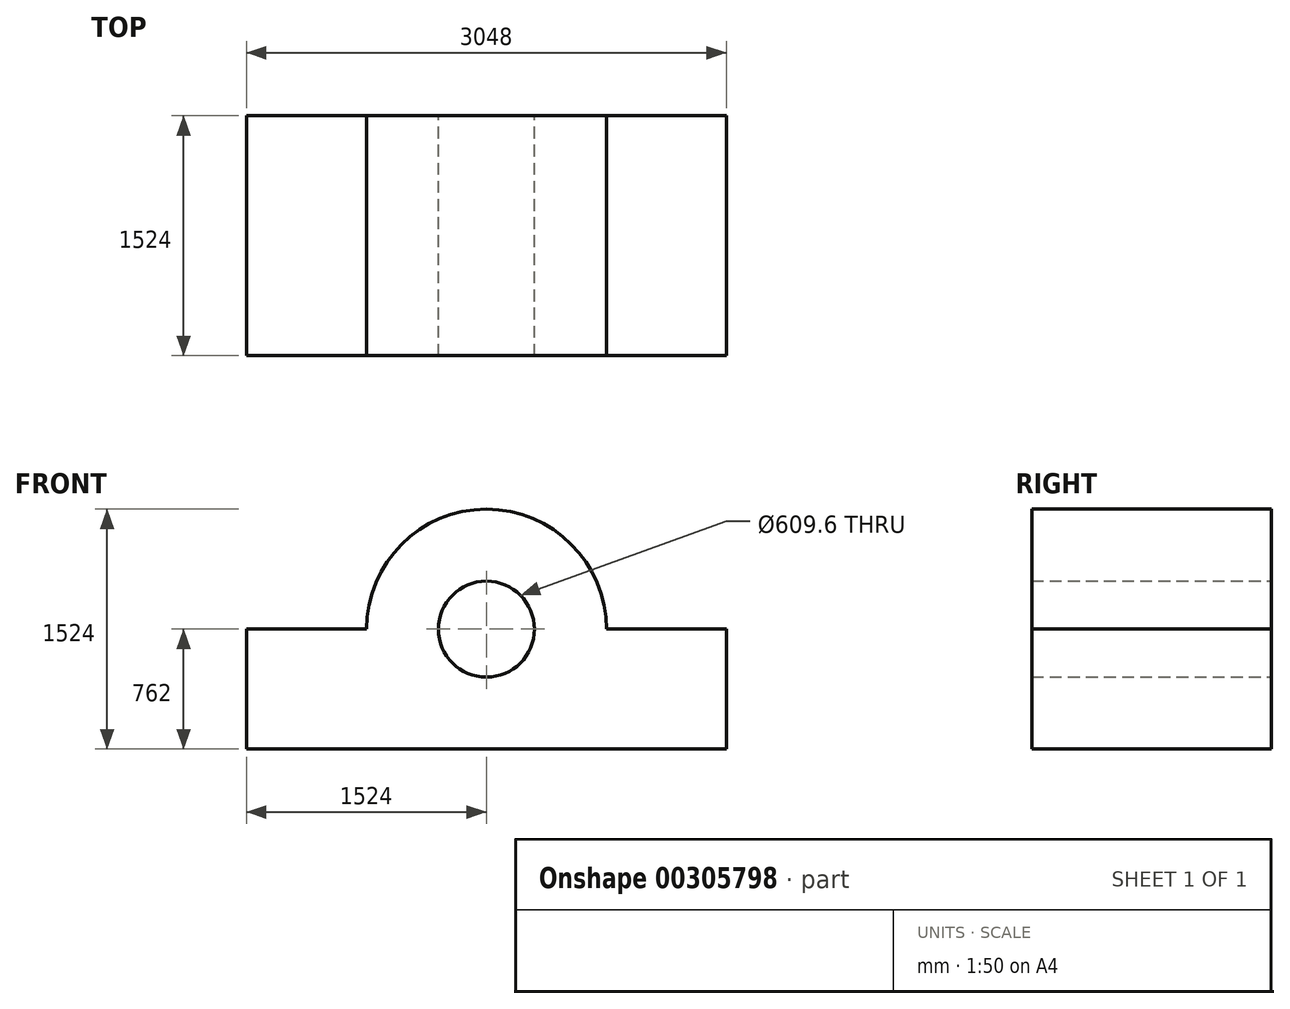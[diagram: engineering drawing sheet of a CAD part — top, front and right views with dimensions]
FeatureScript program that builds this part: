
annotation { "Feature Type Name" : "Feature", "Feature Type Description" : "" }
export const myFeature = defineFeature(function(context is Context, id is Id, definition is map)
    precondition{}
    {
        {
            var Q0;
            Q0=qCreatedBy(makeId("Front.planeOp"),FACE);
            var sketch = newSketch(context, id + "F0", { "sketchPlane" : qUnion([Q0])});
            skCircle(sketch, "E0", {"center": v(0, 0) * mm, "radius": 304.8 * mm});
            skArc(sketch, "E1", {"start": v(762, 0) * mm, "mid": v(0, 762) * mm, "end": v(-762, 0) * mm});
            skLineSegment(sketch, "E2", {"start": v(0, 0) * mm, "end": v(1524, 0) * mm});
            skLineSegment(sketch, "E3", {"start": v(1524, 0) * mm, "end": v(1524, -762) * mm});
            skLineSegment(sketch, "E4", {"start": v(1524, -762) * mm, "end": v(-1524, -762) * mm});
            skLineSegment(sketch, "E5", {"start": v(-1524, -762) * mm, "end": v(-1524, 0) * mm});
            skLineSegment(sketch, "E6", {"start": v(-1524, 0) * mm, "end": v(-762, 0) * mm});
            skSolve(sketch);
        }
        {
            var Q0;
            Q0=makeQuery(id+"F0.imprint","IMPRINT",FACE,{"disambiguationData":[TD([[makeQuery(id+"F0.imprint","IMPRINT",EDGE,{"derivedFrom":sQuery(id+"F0.wireOp",EDGE,"E0")}),-1.0]])]});
            extrude(context, id + "F1", {"entities" : qUnion([Q0]), "depth" : 1524 * mm});
        }
    });
